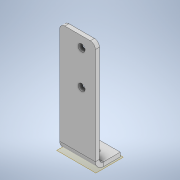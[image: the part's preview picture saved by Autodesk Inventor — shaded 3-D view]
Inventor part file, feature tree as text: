
AUTODESK INVENTOR PART (.ipt)
format: ipt  version: 2020 (Build 240168000, 168)  size: 194,048 bytes
history: native  units: in
note: dims shown in document units (in); Inventor stores cm internally (conversion verified against a paired STEP export)
features: sketch x4, sheet_metal_op x2, hole x2, other x2, chamfer x1
ambient origin geometry x8: Origin, YZ Plane, XZ Plane, XY Plane, X Axis, Y Axis, Z Axis, Center Point
bodies: Solid1 (feature_tree)
feature tree (11):
  sheet_metal_op  "Face1"
  sheet_metal_op  "Fold1"
  hole  "Hole2"  [1 undecoded]
  hole  "Hole3"  [1 undecoded]
  chamfer  "Corner Round1"
  sketch  "Sketch2"  dims[d6=0.1181in d9=0.1181in]
  other  "Plate1"
  sketch  "Sketch3"  dims[d10=0.0591in d11=0.2362in]
  sketch  "Sketch5"  dims[d12=0.1181in]
  sketch  "Sketch6"  dims[d13=90.0deg d14=0.1181in d34=0.2008in d35=0.1575in d36=0.3937in d37=0.2008in d38=0.2362in d39=0.1575in d40=0.0787in d41=90.0deg d42=0.315in d43=0.8108in d44=0.2008in d45=0.2008in d46=1.7717in d47=2.7559in d48=0.3937in d49=0.3937in d50=0.2008in d51=0.2362in d52=0.1575in d53=0.0787in d54=90.0deg d55=0.315in d56=0.8108in d57=0.5979in d58=0.1457in]
  other  "Definition1"
note: 2 required parameter values undecoded (feature->parameter linkage not recoverable at this tier; creation-order binding heuristic only, values carry confidence <= 0.55)
